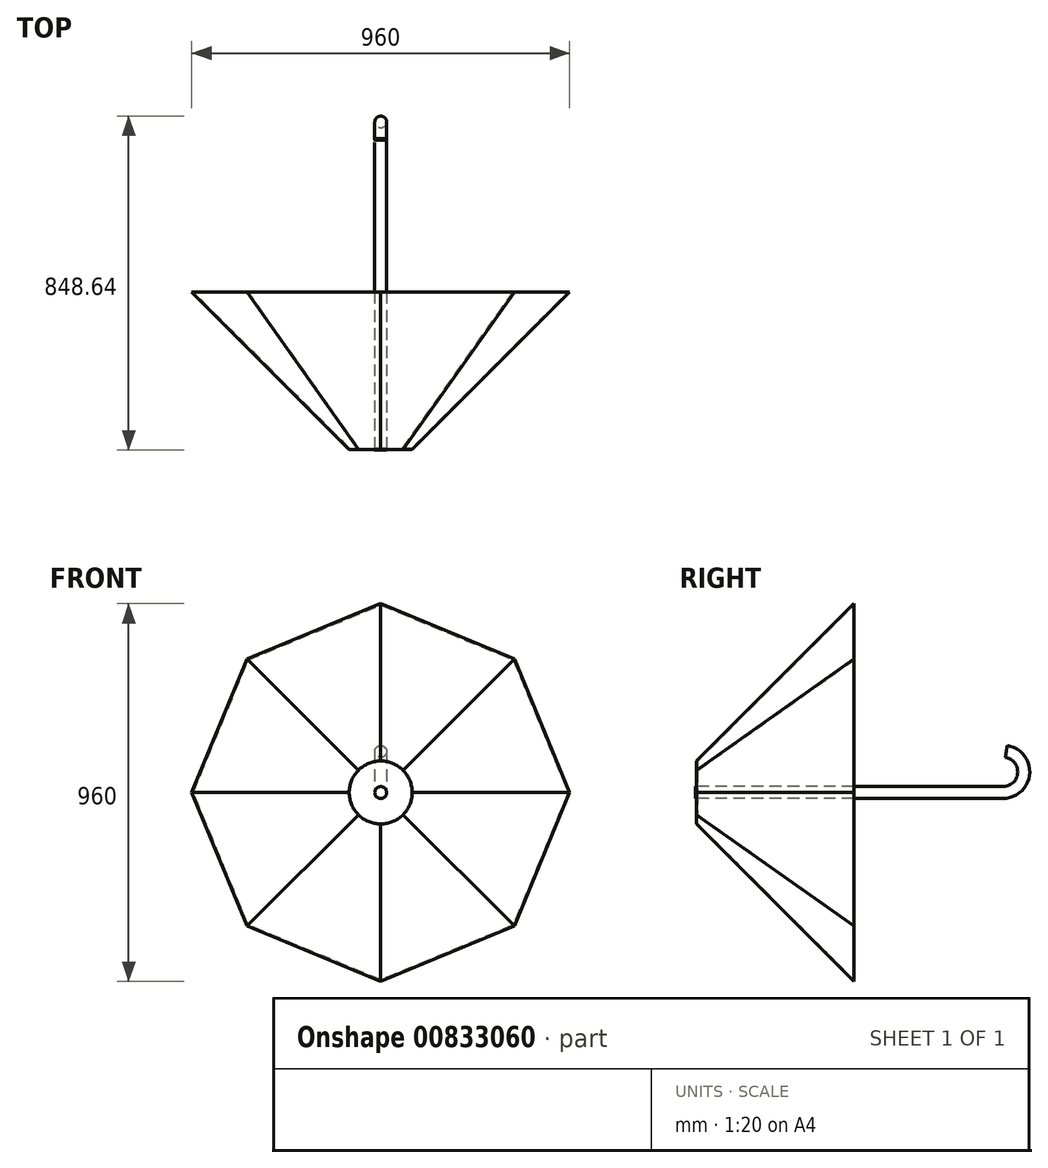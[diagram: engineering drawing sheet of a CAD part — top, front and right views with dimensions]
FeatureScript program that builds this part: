
annotation { "Feature Type Name" : "Feature", "Feature Type Description" : "" }
export const myFeature = defineFeature(function(context is Context, id is Id, definition is map)
    precondition{}
    {
        {
            var Q0;
            Q0=qCreatedBy(makeId("Front.planeOp"),FACE);
            cPlane(context, id + "F0", {"entities" : qUnion([Q0]), "cplaneType" : CPlaneType.OFFSET, "offset" : 400 * mm, "width" : 150 * mm, "height" : 150 * mm});
        }
        {
            var Q0;
            Q0=qCreatedBy(id+"F0.planeOp",FACE);
            var sketch = newSketch(context, id + "F1", { "sketchPlane" : qUnion([Q0])});
            skCircle(sketch, "E0", {"center": v(0, 0) * mm, "radius": 80 * mm});
            skSolve(sketch);
        }
        {
            var Q0;
            Q0=qCreatedBy(makeId("Front.planeOp"),FACE);
            var sketch = newSketch(context, id + "F2", { "sketchPlane" : qUnion([Q0])});
            skCircle(sketch, "E1.cCircle", {"center": v(0, 0) * mm, "radius": 443.46 * mm, "construction": true});
            skLineSegment(sketch, "E1.0", {"start": v(339.41, -339.41) * mm, "end": v(0, -480) * mm});
            skLineSegment(sketch, "E1.1", {"start": v(0, -480) * mm, "end": v(-339.41, -339.41) * mm});
            skLineSegment(sketch, "E1.2", {"start": v(-339.41, -339.41) * mm, "end": v(-480, 0) * mm});
            skLineSegment(sketch, "E1.3", {"start": v(-480, 0) * mm, "end": v(-339.41, 339.41) * mm});
            skLineSegment(sketch, "E1.4", {"start": v(-339.41, 339.41) * mm, "end": v(0, 480) * mm});
            skLineSegment(sketch, "E1.5", {"start": v(0, 480) * mm, "end": v(339.41, 339.41) * mm});
            skLineSegment(sketch, "E1.6", {"start": v(339.41, 339.41) * mm, "end": v(480, 0) * mm});
            skLineSegment(sketch, "E1.7", {"start": v(480, 0) * mm, "end": v(339.41, -339.41) * mm});
            skPoint(sketch, "E1.0.midPoint", {"position": v(169.7, -409.7) * mm});
            skSolve(sketch);
        }
        {
            var Q0;
            Q0=qCreatedBy(makeId("Top.planeOp"),FACE);
            var sketch = newSketch(context, id + "F3", { "sketchPlane" : qUnion([Q0])});
            skArc(sketch, "E2", {"start": v(-480, 0) * mm, "mid": v(-356.36, -276.36) * mm, "end": v(-80, -400) * mm});
            skArc(sketch, "E3.MirrorCS", {"start": v(480, 0) * mm, "mid": v(356.36, -276.36) * mm, "end": v(80, -400) * mm});
            skLineSegment(sketch, "E4", {"start": v(-80, -400) * mm, "end": v(-80, 0) * mm});
            skSolve(sketch);
        }
        {
            var Q0;
            Q0=makeQuery(id+"F1.imprint","IMPRINT",FACE,{"disambiguationData":[TD([[makeQuery(id+"F1.imprint","IMPRINT",EDGE,{"derivedFrom":sQuery(id+"F1.wireOp",EDGE,"E0")}),1.0]])]});
            var Q1;
            Q1=makeQuery(id+"F2.imprint","IMPRINT",FACE,{"disambiguationData":[TD([[makeQuery(id+"F2.imprint","IMPRINT",EDGE,{"derivedFrom":sQuery(id+"F2.wireOp",EDGE,"E1.0")}),-1.0]])]});
            var Q2;
            Q2=sQuery(id+"FqoeVjutgT4pPHW_0.4.F3.wireOp",EDGE,"E2");
            var Q3;
            Q3=sQuery(id+"FqoeVjutgT4pPHW_0.5.F3.wireOp",EDGE,"E2");
            var Q4;
            Q4=sQuery(id+"FqoeVjutgT4pPHW_0.2.F3.wireOp",EDGE,"E3.MirrorCS");
            var Q5;
            Q5=sQuery(id+"FqoeVjutgT4pPHW_0.7.F3.wireOp",EDGE,"E2");
            var Q6;
            Q6=sQuery(id+"FqoeVjutgT4pPHW_0.4.F3.wireOp",EDGE,"E3.MirrorCS");
            var Q7;
            Q7=sQuery(id+"FqoeVjutgT4pPHW_0.1.F3.wireOp",EDGE,"E2");
            var Q8;
            Q8=sQuery(id+"FqoeVjutgT4pPHW_0.2.F3.wireOp",EDGE,"E2");
            var Q9;
            Q9=sQuery(id+"FqoeVjutgT4pPHW_0.7.F3.wireOp",EDGE,"E3.MirrorCS");
            loft(context, id + "F4", {"addGuides" : true, "sheetProfilesArray" : [{ "sheetProfileEntities" : qUnion([Q0]) }, { "sheetProfileEntities" : qUnion([Q1]) }], "guidesArray" : [{ "guideEntities" : qUnion([Q2]), "guideDerivativeType" : LoftGuideDerivativeType.DEFAULT, "guideDerivativeMagnitude" : 1 }, { "guideEntities" : qUnion([Q3]), "guideDerivativeType" : LoftGuideDerivativeType.DEFAULT, "guideDerivativeMagnitude" : 1 }, { "guideEntities" : qUnion([Q4]), "guideDerivativeType" : LoftGuideDerivativeType.DEFAULT, "guideDerivativeMagnitude" : 1 }, { "guideEntities" : qUnion([Q5]), "guideDerivativeType" : LoftGuideDerivativeType.DEFAULT, "guideDerivativeMagnitude" : 1 }, { "guideEntities" : qUnion([Q6]), "guideDerivativeType" : LoftGuideDerivativeType.DEFAULT, "guideDerivativeMagnitude" : 1 }, { "guideEntities" : qUnion([Q7]), "guideDerivativeType" : LoftGuideDerivativeType.DEFAULT, "guideDerivativeMagnitude" : 1 }, { "guideEntities" : qUnion([Q8]), "guideDerivativeType" : LoftGuideDerivativeType.DEFAULT, "guideDerivativeMagnitude" : 1 }, { "guideEntities" : qUnion([Q9]), "guideDerivativeType" : LoftGuideDerivativeType.DEFAULT, "guideDerivativeMagnitude" : 1 }]});
        }
        {
            var Q0;
            Q0=makeQuery(id+"F4.opLoft","CAP_FACE",FACE,{"disambiguationData":[OSD([makeQuery(id+"F2.imprint","IMPRINT",FACE,{"disambiguationData":[TD([[makeQuery(id+"F2.imprint","IMPRINT",EDGE,{"derivedFrom":sQuery(id+"F2.wireOp",EDGE,"E1.0")}),-1.0]])]})])],"isStart":true});
            shell(context, id + "F5", {"entities" : qUnion([Q0]), "thickness" : 2.5 * mm});
        }
        {
            var Q0;
            Q0=makeQuery(id+"F1.imprint","IMPRINT",FACE,{"disambiguationData":[TD([[makeQuery(id+"F1.imprint","IMPRINT",EDGE,{"derivedFrom":sQuery(id+"F1.wireOp",EDGE,"E0")}),1.0]])]});
            var sketch = newSketch(context, id + "F6", { "sketchPlane" : qUnion([Q0])});
            skCircle(sketch, "E5", {"center": v(0, 0) * mm, "radius": 15.1 * mm});
            skSolve(sketch);
        }
        {
            var Q0;
            Q0=qCreatedBy(makeId("Right.planeOp"),FACE);
            var sketch = newSketch(context, id + "F7", { "sketchPlane" : qUnion([Q0])});
            skLineSegment(sketch, "E6", {"start": v(-401.85, 0) * mm, "end": v(379.27, 0) * mm});
            skArc(sketch, "E7", {"start": v(379.27, 0) * mm, "mid": v(431.53, 48.3) * mm, "end": v(387.48, 104.18) * mm});
            skSolve(sketch);
        }
        {
            var Q0;
            Q0=makeQuery(id+"F6.imprint","IMPRINT",FACE,{"disambiguationData":[TD([[makeQuery(id+"F6.imprint","IMPRINT",EDGE,{"derivedFrom":sQuery(id+"F6.wireOp",EDGE,"E5")}),1.0]])]});
            var Q1;
            Q1=sQuery(id+"F7.wireOp",EDGE,"E6");
            var Q2;
            Q2=sQuery(id+"F7.wireOp",EDGE,"E7");
            sweep(context, id + "F8", {"operationType" : NewBodyOperationType.ADD, "profiles" : qUnion([Q0]), "path" : qUnion([Q1, Q2])});
        }
    });
